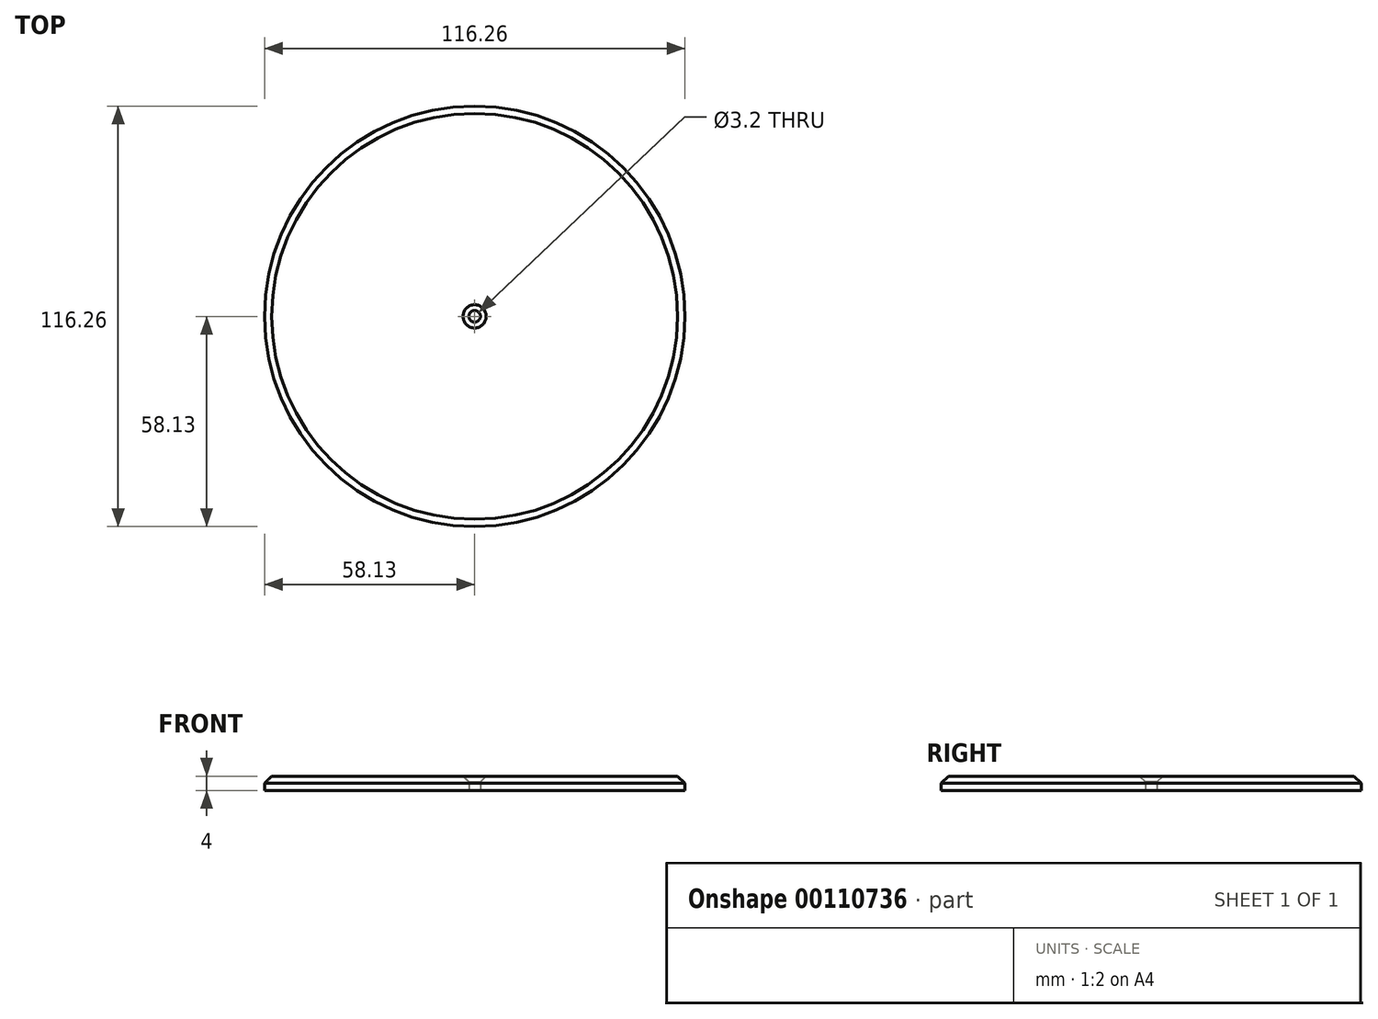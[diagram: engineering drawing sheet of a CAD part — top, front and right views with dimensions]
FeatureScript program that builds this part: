
annotation { "Feature Type Name" : "Feature", "Feature Type Description" : "" }
export const myFeature = defineFeature(function(context is Context, id is Id, definition is map)
    precondition{}
    {
        {
            var Q0;
            Q0=qCreatedBy(makeId("Front.planeOp"),FACE);
            var sketch = newSketch(context, id + "F0", { "sketchPlane" : qUnion([Q0])});
            skLineSegment(sketch, "E0", {"start": v(0, 0) * mm, "end": v(0, 45.75) * mm, "construction": true});
            skLineSegment(sketch, "E1", {"start": v(1.6, 0) * mm, "end": v(58.12, 0) * mm});
            skLineSegment(sketch, "E2", {"start": v(58.12, 0) * mm, "end": v(58.12, 2) * mm});
            skLineSegment(sketch, "E3", {"start": v(58.12, 2) * mm, "end": v(56.12, 4) * mm});
            skLineSegment(sketch, "E4", {"start": v(56.12, 4) * mm, "end": v(3.2, 4) * mm});
            skLineSegment(sketch, "E5", {"start": v(3.2, 4) * mm, "end": v(1.6, 2.4) * mm});
            skLineSegment(sketch, "E6", {"start": v(1.6, 2.4) * mm, "end": v(1.6, 0) * mm});
            skSolve(sketch);
        }
        {
            var Q0;
            Q0=qSketchRegion(id+"F0",true);
            var Q1;
            Q1=sQuery(id+"F0.wireOp",EDGE,"E0");
            revolve(context, id + "F1", {"entities" : qUnion([Q0]), "axis" : qUnion([Q1]), "revolveType" : RevolveType.FULL});
        }
    });
